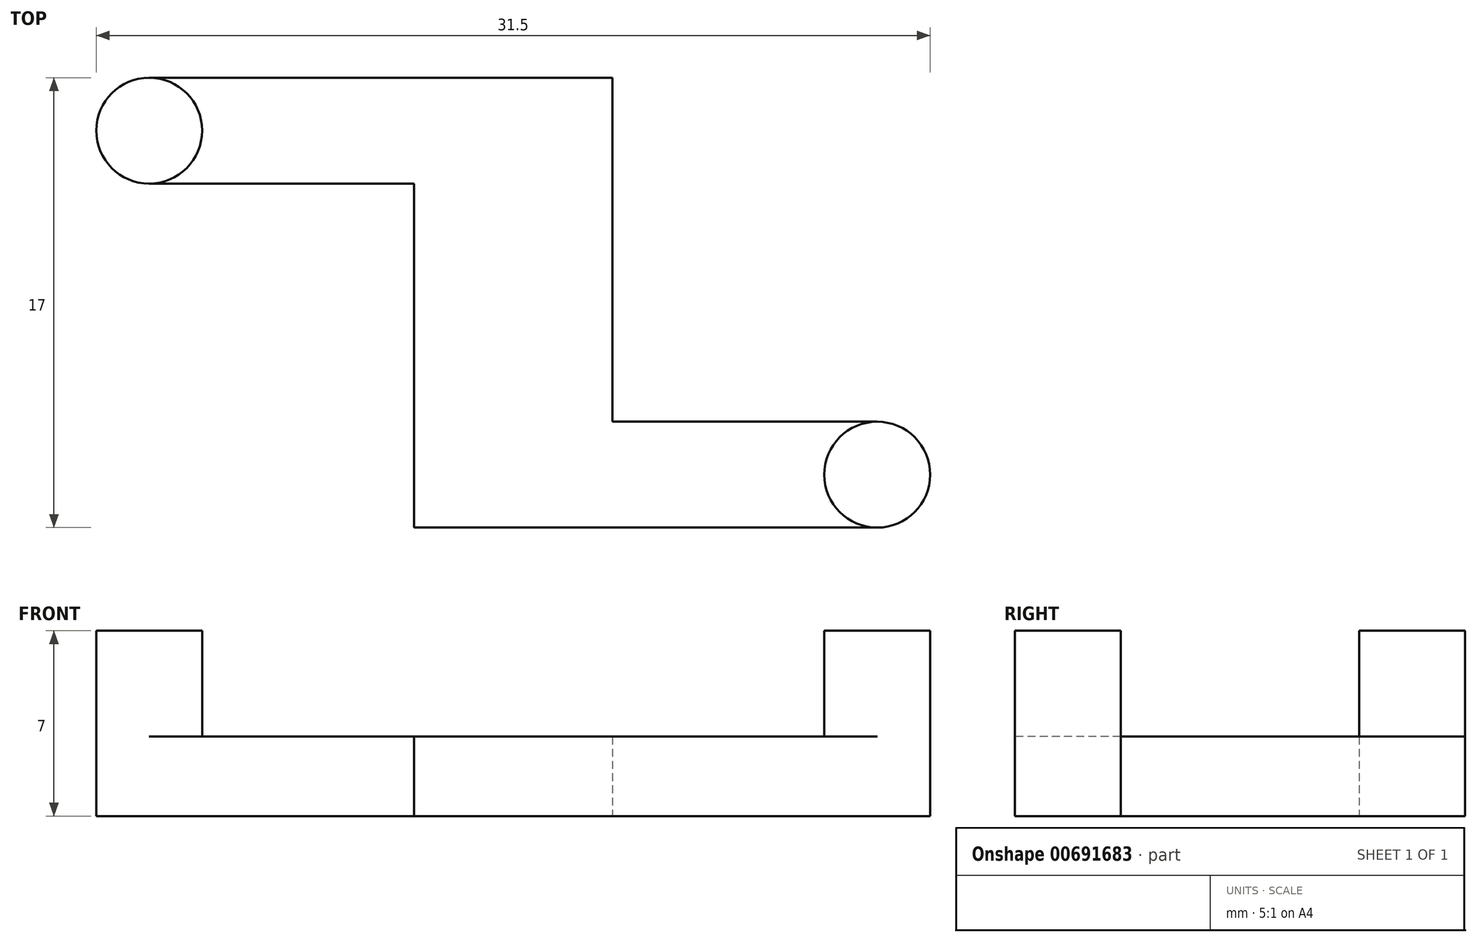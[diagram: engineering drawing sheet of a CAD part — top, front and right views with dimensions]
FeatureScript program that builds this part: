
annotation { "Feature Type Name" : "Feature", "Feature Type Description" : "" }
export const myFeature = defineFeature(function(context is Context, id is Id, definition is map)
    precondition{}
    {
        {
            var Q0;
            Q0=qCreatedBy(makeId("Top.planeOp"),FACE);
            var sketch = newSketch(context, id + "F0", { "sketchPlane" : qUnion([Q0])});
            skLineSegment(sketch, "E0.bottom", {"start": v(3.75, 8.5) * mm, "end": v(-3.75, 8.5) * mm});
            skLineSegment(sketch, "E0.top", {"start": v(3.75, -8.5) * mm, "end": v(-3.75, -8.5) * mm});
            skLineSegment(sketch, "E0.left", {"start": v(3.75, 8.5) * mm, "end": v(3.75, -8.5) * mm});
            skLineSegment(sketch, "E0.right", {"start": v(-3.75, 8.5) * mm, "end": v(-3.75, -8.5) * mm});
            skPoint(sketch, "E0.middle", {"position": v(0, 0) * mm});
            skLineSegment(sketch, "E1.bottom", {"start": v(-3.75, 8.5) * mm, "end": v(-13.75, 8.5) * mm});
            skLineSegment(sketch, "E1.top", {"start": v(-3.75, 4.5) * mm, "end": v(-13.75, 4.5) * mm});
            skLineSegment(sketch, "E1.left", {"start": v(-3.75, 8.5) * mm, "end": v(-3.75, 4.5) * mm});
            skLineSegment(sketch, "E1.right", {"start": v(-13.75, 8.5) * mm, "end": v(-13.75, 4.5) * mm});
            skLineSegment(sketch, "E2.bottom", {"start": v(3.75, -8.5) * mm, "end": v(13.75, -8.5) * mm});
            skLineSegment(sketch, "E2.top", {"start": v(3.75, -4.5) * mm, "end": v(13.75, -4.5) * mm});
            skLineSegment(sketch, "E2.left", {"start": v(3.75, -8.5) * mm, "end": v(3.75, -4.5) * mm});
            skLineSegment(sketch, "E2.right", {"start": v(13.75, -8.5) * mm, "end": v(13.75, -4.5) * mm});
            skCircle(sketch, "E3", {"center": v(-13.75, 6.5) * mm, "radius": 2 * mm});
            skCircle(sketch, "E4", {"center": v(13.75, -6.5) * mm, "radius": 2 * mm});
            skSolve(sketch);
        }
        {
            var Q0;
            {var subQ1=sQuery(id+"F0.wireOp",EDGE,"E1.right");var subQ3=sQuery(id+"F0.wireOp",EDGE,"E3");var subQ4=makeQuery(id+"F0.imprint","INTERSECT",VERTEX,{"disambiguationData":[OD(0.0)],"derivedFrom":[subQ1,subQ3]});Q0=makeQuery(id+"F0.imprint","IMPRINT",FACE,{"disambiguationData":[TD([[makeQuery(id+"F0.imprint","IMPRINT",EDGE,{"disambiguationData":[TD([[subQ4,1.0]])],"derivedFrom":subQ3}),-1.0]])]});}
            var Q1;
            {var subQ0=sQuery(id+"F0.wireOp",EDGE,"E1.bottom");Q1=makeQuery(id+"F0.imprint","IMPRINT",FACE,{"disambiguationData":[TD([[makeQuery(id+"F0.imprint","IMPRINT",EDGE,{"derivedFrom":subQ0}),1.0]])]});}
            var Q2;
            Q2=makeQuery(id+"F0.imprint","IMPRINT",FACE,{"disambiguationData":[TD([[makeQuery(id+"F0.imprint","IMPRINT",EDGE,{"derivedFrom":sQuery(id+"F0.wireOp",EDGE,"E0.bottom")}),1.0]])]});
            var Q3;
            {var subQ0=sQuery(id+"F0.wireOp",EDGE,"E2.bottom");Q3=makeQuery(id+"F0.imprint","IMPRINT",FACE,{"disambiguationData":[TD([[makeQuery(id+"F0.imprint","IMPRINT",EDGE,{"derivedFrom":subQ0}),1.0]])]});}
            var Q4;
            {var subQ1=sQuery(id+"F0.wireOp",EDGE,"E2.right");var subQ3=sQuery(id+"F0.wireOp",EDGE,"E4");var subQ4=makeQuery(id+"F0.imprint","INTERSECT",VERTEX,{"disambiguationData":[OD(0.0)],"derivedFrom":[subQ1,subQ3]});Q4=makeQuery(id+"F0.imprint","IMPRINT",FACE,{"disambiguationData":[TD([[makeQuery(id+"F0.imprint","IMPRINT",EDGE,{"disambiguationData":[TD([[subQ4,1.0]])],"derivedFrom":subQ3}),-1.0]])]});}
            var Q5;
            {var subQ1=sQuery(id+"F0.wireOp",EDGE,"E2.right");var subQ3=sQuery(id+"F0.wireOp",EDGE,"E4");var subQ4=makeQuery(id+"F0.imprint","INTERSECT",VERTEX,{"disambiguationData":[OD(0.0)],"derivedFrom":[subQ1,subQ3]});Q5=makeQuery(id+"F0.imprint","IMPRINT",FACE,{"disambiguationData":[TD([[makeQuery(id+"F0.imprint","IMPRINT",EDGE,{"disambiguationData":[TD([[subQ4,-1.0]])],"derivedFrom":subQ3}),-1.0]])]});}
            var Q6;
            {var subQ1=sQuery(id+"F0.wireOp",EDGE,"E1.right");var subQ3=sQuery(id+"F0.wireOp",EDGE,"E3");var subQ4=makeQuery(id+"F0.imprint","INTERSECT",VERTEX,{"disambiguationData":[OD(0.0)],"derivedFrom":[subQ1,subQ3]});Q6=makeQuery(id+"F0.imprint","IMPRINT",FACE,{"disambiguationData":[TD([[makeQuery(id+"F0.imprint","IMPRINT",EDGE,{"disambiguationData":[TD([[subQ4,-1.0]])],"derivedFrom":subQ3}),-1.0]])]});}
            var Q7;
            {var subQ0=sQuery(id+"F0.wireOp",EDGE,"E4");var subQ1=sQuery(id+"F0.wireOp",EDGE,"E2.right");var subQ2=makeQuery(id+"F0.imprint","INTERSECT",VERTEX,{"disambiguationData":[OD(0.0)],"derivedFrom":[subQ1,subQ0]});Q7=makeQuery(id+"F0.imprint","IMPRINT",FACE,{"disambiguationData":[TD([[makeQuery(id+"F0.imprint","IMPRINT",EDGE,{"disambiguationData":[TD([[subQ2,-1.0]])],"derivedFrom":subQ1}),-1.0]])]});}
            var Q8;
            {var subQ0=sQuery(id+"F0.wireOp",EDGE,"E4");var subQ1=sQuery(id+"F0.wireOp",EDGE,"E2.right");var subQ2=makeQuery(id+"F0.imprint","INTERSECT",VERTEX,{"disambiguationData":[OD(0.0)],"derivedFrom":[subQ1,subQ0]});Q8=makeQuery(id+"F0.imprint","IMPRINT",FACE,{"disambiguationData":[TD([[makeQuery(id+"F0.imprint","IMPRINT",EDGE,{"disambiguationData":[TD([[subQ2,-1.0]])],"derivedFrom":subQ1}),1.0]])]});}
            var Q9;
            {var subQ0=sQuery(id+"F0.wireOp",EDGE,"E3");var subQ1=sQuery(id+"F0.wireOp",EDGE,"E1.right");var subQ2=makeQuery(id+"F0.imprint","INTERSECT",VERTEX,{"disambiguationData":[OD(0.0)],"derivedFrom":[subQ1,subQ0]});Q9=makeQuery(id+"F0.imprint","IMPRINT",FACE,{"disambiguationData":[TD([[makeQuery(id+"F0.imprint","IMPRINT",EDGE,{"disambiguationData":[TD([[subQ2,-1.0]])],"derivedFrom":subQ1}),-1.0]])]});}
            var Q10;
            {var subQ0=sQuery(id+"F0.wireOp",EDGE,"E3");var subQ1=sQuery(id+"F0.wireOp",EDGE,"E1.right");var subQ2=makeQuery(id+"F0.imprint","INTERSECT",VERTEX,{"disambiguationData":[OD(0.0)],"derivedFrom":[subQ1,subQ0]});Q10=makeQuery(id+"F0.imprint","IMPRINT",FACE,{"disambiguationData":[TD([[makeQuery(id+"F0.imprint","IMPRINT",EDGE,{"disambiguationData":[TD([[subQ2,-1.0]])],"derivedFrom":subQ1}),1.0]])]});}
            extrude(context, id + "F1", {"entities" : qUnion([Q0, Q1, Q2, Q3, Q4, Q5, Q6, Q7, Q8, Q9, Q10]), "depth" : 3 * mm, "offsetDistance" : 25 * mm});
        }
        {
            var Q0;
            {var subQ0=sQuery(id+"F0.wireOp",EDGE,"E4");var subQ1=sQuery(id+"F0.wireOp",EDGE,"E2.right");var subQ2=makeQuery(id+"F0.imprint","INTERSECT",VERTEX,{"disambiguationData":[OD(0.0)],"derivedFrom":[subQ1,subQ0]});Q0=makeQuery(id+"F0.imprint","IMPRINT",FACE,{"disambiguationData":[TD([[makeQuery(id+"F0.imprint","IMPRINT",EDGE,{"disambiguationData":[TD([[subQ2,-1.0]])],"derivedFrom":subQ1}),-1.0]])]});}
            var Q1;
            {var subQ0=sQuery(id+"F0.wireOp",EDGE,"E4");var subQ1=sQuery(id+"F0.wireOp",EDGE,"E2.right");var subQ2=makeQuery(id+"F0.imprint","INTERSECT",VERTEX,{"disambiguationData":[OD(0.0)],"derivedFrom":[subQ1,subQ0]});Q1=makeQuery(id+"F0.imprint","IMPRINT",FACE,{"disambiguationData":[TD([[makeQuery(id+"F0.imprint","IMPRINT",EDGE,{"disambiguationData":[TD([[subQ2,-1.0]])],"derivedFrom":subQ1}),1.0]])]});}
            var Q2;
            {var subQ0=sQuery(id+"F0.wireOp",EDGE,"E3");var subQ1=sQuery(id+"F0.wireOp",EDGE,"E1.right");var subQ2=makeQuery(id+"F0.imprint","INTERSECT",VERTEX,{"disambiguationData":[OD(0.0)],"derivedFrom":[subQ1,subQ0]});Q2=makeQuery(id+"F0.imprint","IMPRINT",FACE,{"disambiguationData":[TD([[makeQuery(id+"F0.imprint","IMPRINT",EDGE,{"disambiguationData":[TD([[subQ2,-1.0]])],"derivedFrom":subQ1}),1.0]])]});}
            var Q3;
            {var subQ0=sQuery(id+"F0.wireOp",EDGE,"E3");var subQ1=sQuery(id+"F0.wireOp",EDGE,"E1.right");var subQ2=makeQuery(id+"F0.imprint","INTERSECT",VERTEX,{"disambiguationData":[OD(0.0)],"derivedFrom":[subQ1,subQ0]});Q3=makeQuery(id+"F0.imprint","IMPRINT",FACE,{"disambiguationData":[TD([[makeQuery(id+"F0.imprint","IMPRINT",EDGE,{"disambiguationData":[TD([[subQ2,-1.0]])],"derivedFrom":subQ1}),-1.0]])]});}
            extrude(context, id + "F2", {"entities" : qUnion([Q0, Q1, Q2, Q3]), "operationType" : NewBodyOperationType.ADD, "depth" : 7 * mm, "offsetDistance" : 25 * mm});
        }
    });
